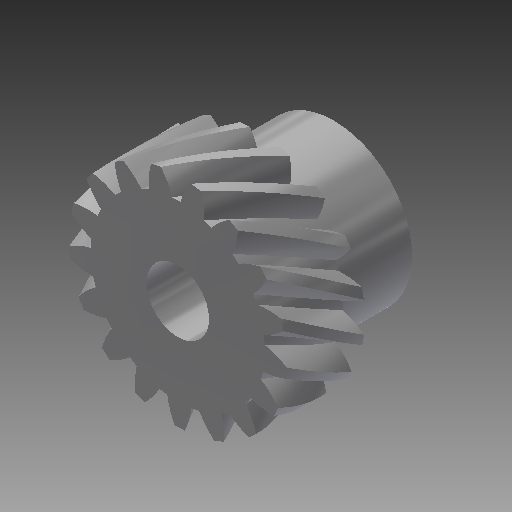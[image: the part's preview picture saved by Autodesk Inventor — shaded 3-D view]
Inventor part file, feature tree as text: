
AUTODESK INVENTOR PART (.ipt)
format: ipt  version: 2018 (Build 220112000, 112)  size: 499,712 bytes
history: native  units: mm (DEFAULTED — no unit token found)
features: extrude x4, sketch x4, plane x3, other x3
ambient origin geometry x8: Origin, YZ Plane, XZ Plane, XY Plane, X Axis, Y Axis, Z Axis, Center Point
bodies: Solid1 (feature_tree)
feature tree (14):
  extrude  "Extrusion1"  Depth=10.16mm TaperAngle=0.0deg
  plane  "Work Plane1"
  plane  "Work Plane2"
  plane  "Work Plane3"
  other  "Spur Gear"
  extrude  "Extrusion2"  Depth=76.2mm TaperAngle=0.0deg
  extrude  "Extrusion4"  TaperAngle=0.0deg  [1 undecoded]
  extrude  "Extrusion5"  Depth=5.08mm
  sketch  "Sketch1"  dims[d0=14.176796mm d1=10.16mm d2=0.0mm]
  sketch  "Sketch2"  dims[d3=12.552326mm d4=76.2mm d5=0.0mm]
  other  "Srf1"
  sketch  "Sketch5"  dims[d6=0.0mm d7=1.847996mm d9=0.0mm]
  sketch  "Sketch6"  dims[d14=0.0mm d15=31.75mm d16=0.0mm d17=0.0mm d18=0.0mm d19=31.75mm d21=25.4mm d22=0.0mm d28=3.048mm d30=10.16mm d31=0.0mm d32=2.54mm d33=10.16mm d34=15.24mm d35=5.08mm d36=0.0mm d37=4.064mm]
  other  "Pitch Diameter"
note: 1 required parameter value undecoded (feature->parameter linkage not recoverable at this tier; creation-order binding heuristic only, values carry confidence <= 0.55)
